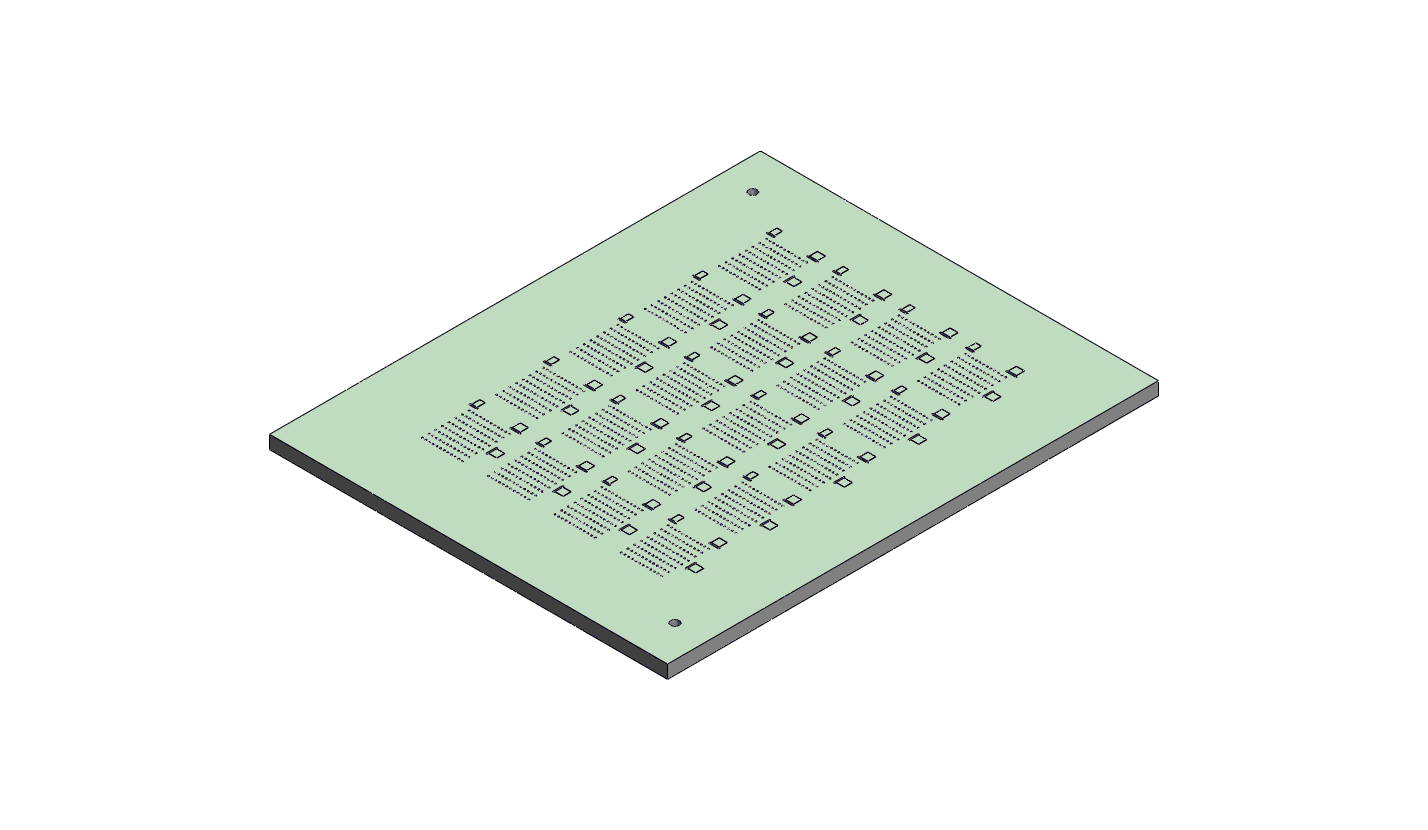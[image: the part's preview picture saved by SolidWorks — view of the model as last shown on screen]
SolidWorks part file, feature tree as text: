
SOLIDWORKS PART (.sldprt)
format: sldprt  version: not decoded by parser v0  size: 2,575,872 bytes
history: native  units: mm
features: sketch x5, cut_extrude x3, pattern_linear x3, extrude x2, material x1 (+11 scaffold rows collapsed)
feature tree (25):
  scaffold x11  (default folders/planes/origin — collapsed)
  material  "6061 Alloy"
  sketch  "Sketch1"  dims[c1.D1=20.24mm c1.D2=22.73mm c1.D3=25.4mm c1.D4=25.4mm c1.D5=150.0mm c1.D6=185.0mm c2.D3=37.5mm c2.D4=56.0mm]
  extrude  "Extrude1"  Depth=5mm
  sketch  "Sketch2"  dims[c1.D1=3.0mm c1.D2=3.0mm c1.D3=9.0mm c1.D4=1.0mm c2.D1=3.0mm c2.D3=2.0mm c2.D5=1.0mm]
  extrude  "Extrude2"  Depth=0.1mm
  sketch  "Sketch3"  dims[D1=0.635mm D2=0.2mm D3=0.2mm]
  cut_extrude  "Extrude3"  Depth=0.5mm
  sketch  "Sketch4"  dims[D2=0.508mm D1=~2.525556mm]
  cut_extrude  "Extrude4"  [1 undecoded]
  pattern_linear  "LPattern1"  Count1=12 Count2=1 Spacing1=1.380808mm Spacing2=50mm
  pattern_linear  "LPattern2"  Count1=4 Count2=1 Spacing1=25mm Spacing2=50mm
  pattern_linear  "LPattern3"  Count1=5 Count2=1 Spacing1=28mm Spacing2=50mm
  sketch  "Sketch5"  dims[D2=3.175mm D1=200.0mm]
  cut_extrude  "Extrude5"  [1 undecoded]
decode coverage: 11 of 13 modeling features carry decoded parameters
note: ~ marks probable driven/reference dimensions
note: 2 parameter values undecoded
note: suppression state not decoded; provenance and decode notes live in map.json
